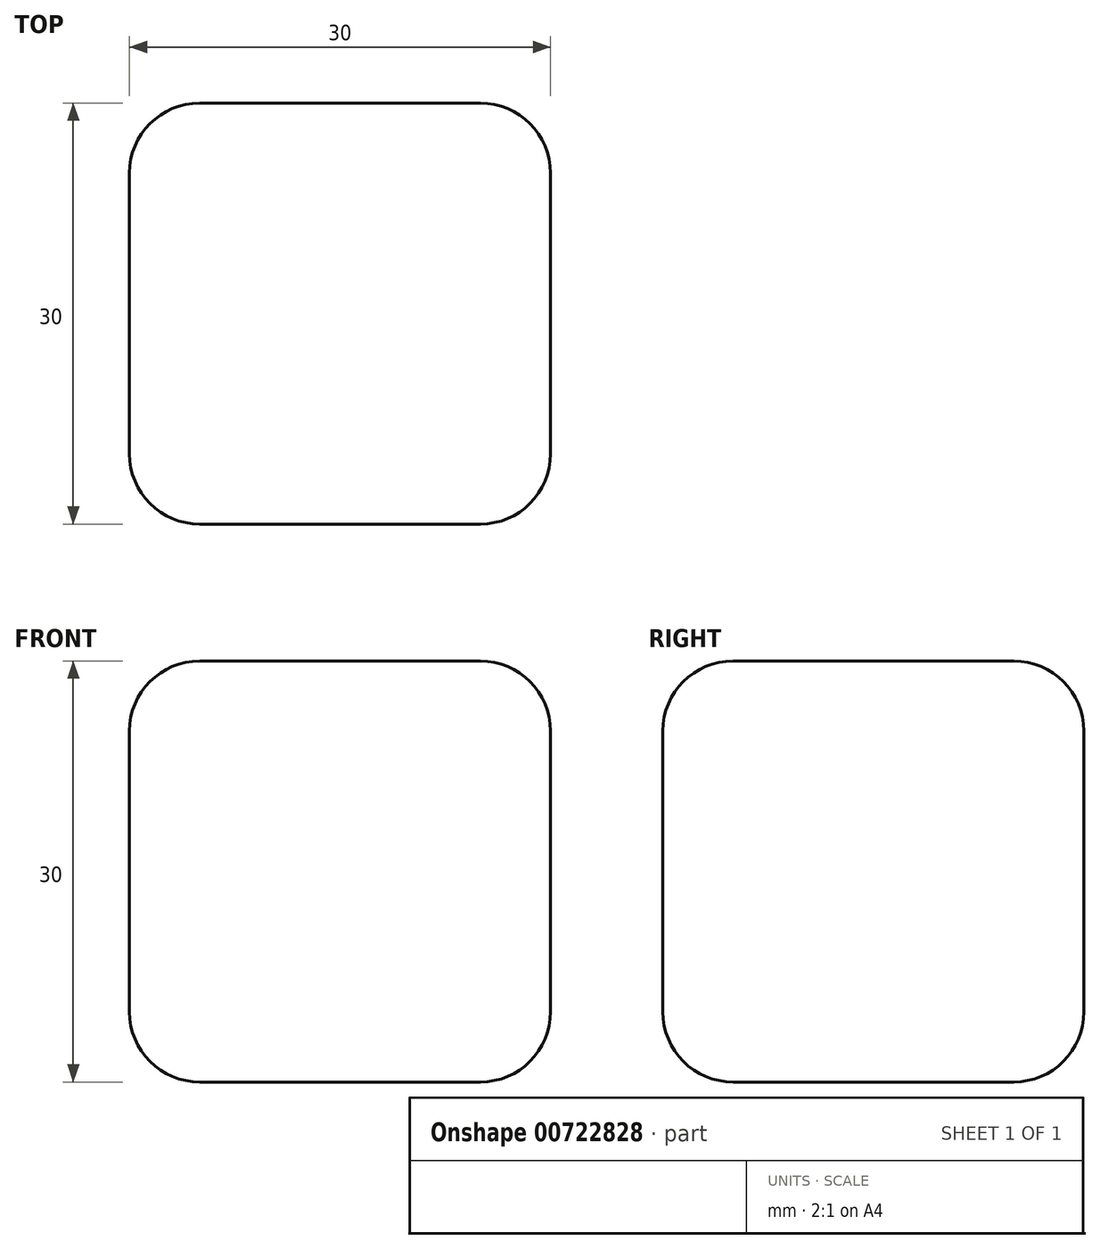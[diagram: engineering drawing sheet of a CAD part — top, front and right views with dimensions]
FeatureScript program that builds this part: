
annotation { "Feature Type Name" : "Feature", "Feature Type Description" : "" }
export const myFeature = defineFeature(function(context is Context, id is Id, definition is map)
    precondition{}
    {
        {
            var Q0;
            Q0=qCreatedBy(makeId("Right.planeOp"),FACE);
            var sketch = newSketch(context, id + "F0", { "sketchPlane" : qUnion([Q0])});
            skLineSegment(sketch, "E0.bottom", {"start": v(9.52, 17.12) * mm, "end": v(-20.48, 17.12) * mm});
            skLineSegment(sketch, "E0.top", {"start": v(9.52, -12.88) * mm, "end": v(-20.48, -12.88) * mm});
            skLineSegment(sketch, "E0.left", {"start": v(9.52, 17.12) * mm, "end": v(9.52, -12.88) * mm});
            skLineSegment(sketch, "E0.right", {"start": v(-20.48, 17.12) * mm, "end": v(-20.48, -12.88) * mm});
            skSolve(sketch);
        }
        {
            var Q0;
            Q0=makeQuery(id+"F0.imprint","IMPRINT",FACE,{"disambiguationData":[TD([[makeQuery(id+"F0.imprint","IMPRINT",EDGE,{"derivedFrom":sQuery(id+"F0.wireOp",EDGE,"E0.bottom")}),1.0]])]});
            extrude(context, id + "F1", {"entities" : qUnion([Q0]), "depth" : 30 * mm, "offsetDistance" : 25 * mm});
        }
        {
            var Q0;
            Q0=makeQuery(id+"F1.opExtrude","CAP_FACE",FACE,{"disambiguationData":[OSD([sQuery(id+"F0.wireOp",EDGE,"E0.bottom"),sQuery(id+"F0.wireOp",EDGE,"E0.top"),sQuery(id+"F0.wireOp",EDGE,"E0.left"),sQuery(id+"F0.wireOp",EDGE,"E0.right")])],"isStart":false});
            fillet(context, id + "F2", {"entities" : qUnion([Q0]), "radius" : 5 * mm, "tangentPropagation" : true, "allowEdgeOverflow" : false});
        }
        {
            var Q0;
            Q0=makeQuery(id+"F1.opExtrude","SWEPT_FACE",FACE,{"disambiguationData":[OSD([sQuery(id+"F0.wireOp",EDGE,"E0.left")])]});
            fillet(context, id + "F3", {"entities" : qUnion([Q0]), "radius" : 5 * mm, "tangentPropagation" : true, "allowEdgeOverflow" : false});
        }
        {
            var Q0;
            Q0=makeQuery(id+"F1.opExtrude","SWEPT_FACE",FACE,{"disambiguationData":[OSD([sQuery(id+"F0.wireOp",EDGE,"E0.right")])]});
            fillet(context, id + "F4", {"entities" : qUnion([Q0]), "radius" : 5 * mm, "tangentPropagation" : true, "allowEdgeOverflow" : false});
        }
        {
            var Q0;
            Q0=makeQuery(id+"F1.opExtrude","SWEPT_FACE",FACE,{"disambiguationData":[OSD([sQuery(id+"F0.wireOp",EDGE,"E0.bottom")])]});
            fillet(context, id + "F5", {"entities" : qUnion([Q0]), "radius" : 5 * mm, "tangentPropagation" : true, "allowEdgeOverflow" : false});
        }
        {
            var Q0;
            Q0=makeQuery(id+"F1.opExtrude","CAP_FACE",FACE,{"disambiguationData":[OSD([sQuery(id+"F0.wireOp",EDGE,"E0.bottom"),sQuery(id+"F0.wireOp",EDGE,"E0.top"),sQuery(id+"F0.wireOp",EDGE,"E0.left"),sQuery(id+"F0.wireOp",EDGE,"E0.right")])],"isStart":true});
            fillet(context, id + "F6", {"entities" : qUnion([Q0]), "radius" : 5 * mm, "tangentPropagation" : true, "allowEdgeOverflow" : false});
        }
    });
